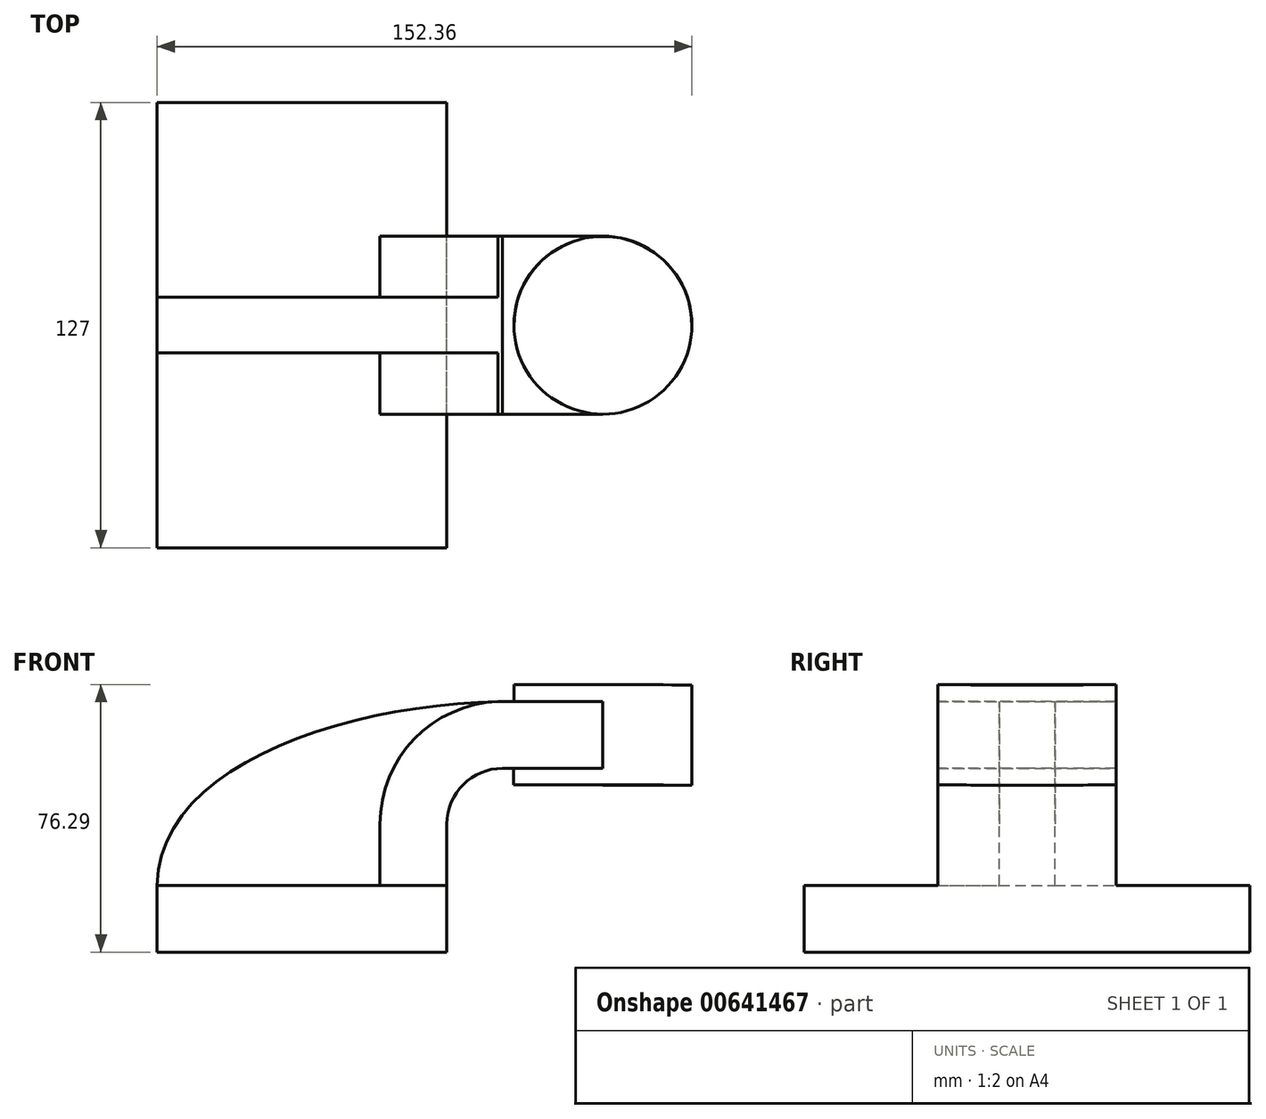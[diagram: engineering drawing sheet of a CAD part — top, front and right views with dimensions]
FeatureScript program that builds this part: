
annotation { "Feature Type Name" : "Feature", "Feature Type Description" : "" }
export const myFeature = defineFeature(function(context is Context, id is Id, definition is map)
    precondition{}
    {
        {
            var Q0;
            Q0=qCreatedBy(makeId("Front.planeOp"),FACE);
            var sketch = newSketch(context, id + "F0", { "sketchPlane" : qUnion([Q0])});
            skLineSegment(sketch, "E0.bottom", {"start": v(-41.28, 9.52) * mm, "end": v(41.27, 9.53) * mm});
            skLineSegment(sketch, "E0.top", {"start": v(-41.28, -9.53) * mm, "end": v(41.28, -9.53) * mm});
            skLineSegment(sketch, "E0.left", {"start": v(-41.28, 9.52) * mm, "end": v(-41.28, -9.53) * mm});
            skLineSegment(sketch, "E0.right", {"start": v(41.27, 9.53) * mm, "end": v(41.28, -9.52) * mm});
            skPoint(sketch, "E0.middle", {"position": v(0, 0) * mm});
            skLineSegment(sketch, "E1.bottom", {"start": v(111.08, 38.1) * mm, "end": v(60.28, 38.1) * mm});
            skLineSegment(sketch, "E1.top", {"start": v(111.08, 66.68) * mm, "end": v(60.28, 66.68) * mm});
            skLineSegment(sketch, "E1.left", {"start": v(111.08, 38.1) * mm, "end": v(111.08, 66.67) * mm});
            skLineSegment(sketch, "E1.right", {"start": v(60.28, 38.1) * mm, "end": v(60.28, 66.67) * mm});
            skPoint(sketch, "E1.middle", {"position": v(85.68, 52.39) * mm});
            skLineSegment(sketch, "E2", {"start": v(41.27, 9.53) * mm, "end": v(41.27, 27) * mm});
            skArc(sketch, "E3", {"start": v(41.27, 27) * mm, "mid": v(45.92, 38.23) * mm, "end": v(57.15, 42.88) * mm});
            skLineSegment(sketch, "E4", {"start": v(57.15, 42.88) * mm, "end": v(85.72, 42.88) * mm});
            skLineSegment(sketch, "E5.0", {"start": v(57.15, 61.93) * mm, "end": v(85.72, 61.93) * mm});
            skArc(sketch, "E5.1", {"start": v(22.22, 27) * mm, "mid": v(32.45, 51.7) * mm, "end": v(57.15, 61.93) * mm});
            skLineSegment(sketch, "E5.2", {"start": v(22.22, 9.53) * mm, "end": v(22.22, 27) * mm});
            skLineSegment(sketch, "E6", {"start": v(85.68, 38.1) * mm, "end": v(85.72, 66.68) * mm});
            skFitSpline(sketch, "E7", {"points": [v(-41.28, 9.52) * mm, v(57.15, 61.93) * mm], "startDerivative": vector(1.13, 103.18) * mm, "endDerivative": vector(132.99, 1.95) * mm});
            skSolve(sketch);
        }
        {
            var Q0;
            Q0=makeQuery(id+"F0.imprint","IMPRINT",FACE,{"disambiguationData":[TD([[makeQuery(id+"F0.imprint","IMPRINT",EDGE,{"derivedFrom":sQuery(id+"F0.wireOp",EDGE,"E0.top")}),1.0]])]});
            extrude(context, id + "F1", {"entities" : qUnion([Q0]), "endBound" : BoundingType.SYMMETRIC, "depth" : 127 * mm, "offsetDistance" : 25.4 * mm});
        }
        {
            var Q0;
            {var subQ1=sQuery(id+"F0.wireOp",EDGE,"E2");Q0=makeQuery(id+"F0.imprint","IMPRINT",FACE,{"disambiguationData":[TD([[makeQuery(id+"F0.imprint","IMPRINT",EDGE,{"derivedFrom":subQ1}),1.0]])]});}
            var Q1;
            {var subQ0=sQuery(id+"F0.wireOp",EDGE,"E4");var subQ1=sQuery(id+"F0.wireOp",EDGE,"E1.right");var subQ2=makeQuery(id+"F0.imprint","INTERSECT",VERTEX,{"derivedFrom":[subQ1,subQ0]});Q1=makeQuery(id+"F0.imprint","IMPRINT",FACE,{"disambiguationData":[TD([[makeQuery(id+"F0.imprint","IMPRINT",EDGE,{"disambiguationData":[TD([[subQ2,-1.0]])],"derivedFrom":subQ1}),-1.0]])]});}
            extrude(context, id + "F2", {"entities" : qUnion([Q0, Q1]), "operationType" : NewBodyOperationType.ADD, "endBound" : BoundingType.SYMMETRIC, "depth" : 50.8 * mm, "offsetDistance" : 25.4 * mm});
        }
        {
            var Q0;
            {var subQ3=sQuery(id+"F0.wireOp",EDGE,"E5.2");Q0=makeQuery(id+"F0.imprint","IMPRINT",FACE,{"disambiguationData":[TD([[makeQuery(id+"F0.imprint","IMPRINT",EDGE,{"derivedFrom":subQ3}),1.0]])]});}
            extrude(context, id + "F3", {"entities" : qUnion([Q0]), "operationType" : NewBodyOperationType.ADD, "endBound" : BoundingType.SYMMETRIC, "depth" : 15.88 * mm, "offsetDistance" : 25.4 * mm});
        }
        {
            var Q0;
            {var subQ0=sQuery(id+"F0.wireOp",EDGE,"E1.left");Q0=makeQuery(id+"F0.imprint","IMPRINT",FACE,{"disambiguationData":[TD([[makeQuery(id+"F0.imprint","IMPRINT",EDGE,{"derivedFrom":subQ0}),1.0]])]});}
            var Q1;
            Q1=sQuery(id+"F0.wireOp",EDGE,"E6");
            revolve(context, id + "F4", {"operationType" : NewBodyOperationType.ADD, "entities" : qUnion([Q0]), "axis" : qUnion([Q1]), "revolveType" : RevolveType.FULL});
        }
    });
